# Revit family: P350181-031
name_source: partatom
category: Lighting Fixtures
units: mm (PartAtom-declared; Revit-internal decimal feet)

## family parameters
Cut with Voids When Loaded = No
Host = Face
Light Source = No
OmniClass Number = 23.80.70.11.14.11
OmniClass Title = Downlights
Part Type = Normal
Room Calculation Point = No
Round Connector Dimension = Use Diameter
Shared = No

## types (1)
- P350181-031
    Apparent Load = 60 VA
    Ballast = Paint - Hubbell - Carbon Black
    Certifications = • cCSAus certified to UL 1598
• Wall Mount: Suitable for wet locations
• Surface & Pendant Mount: Suitable for wet
locations under covered ceiling
• Cord Mount and all Wall Wash: Suitable for
damp locations
    Default Elevation = 48 "
    Description = Stockbrace Collection Three-Light Matte Black and Clear Glass Farmhouse Style Flush Mount Ceiling Light
    Features = Application: Inspired by traditional post-and-beam construction, the Stockbrace Collection 3-Light Matte Black Clear Glass Farmhouse Flush Mount Ceiling Light is ideal for any hallway, stairwell, entryway, kitchen, or sitting room.
Styles: Perfect for modern farmhouse style settings.
Finish: The round ceiling plate and stately light bases are coated in a classic matte black finish.
Materials: Constructed from steel to ensure a long product lifespan.
Glass/Shade: Light sources illuminate clear glass shades to complete the clean design.
Bulbs: For ideal illumination, use 3 medium base bulbs that are sold separately (60w max - LED/CFL/incandescent). Compatible with dimmable bulbs.
Dimensions: Measures 12-1/2-inch diameter by 10-inch height.
Certifications: cCSAus damp location listed.
Pairs With: Pairs with the Briarwood, Lockhart, and Clarion collections from Progress Lighting.
Warranty: Our 1-Year Limited Warranty guarantees your complete satisfaction with your purchase and includes professional after-sales customer service support.
    Glass = Paint - Hubbell - White Texture
    Gold = Hubbell - Gold
    Housing Material = Paint - Hubbell - Textured Camera Black
    Lamp = LED/CFL/incandescent
    Manufacturer = Progress Lighting
    Model = P350181-031
    Product Documentation Link = https://hubbellcdn.com
    Product Page URL = https://www.hubbell.com
    Reflector = Glass - Hubbell - Glass
    URL = https://www.hubbell.com
    Voltage = 120 V
    Warranty = 1 year warranty
    Wattage Comments = 60W

## geometry (parser evidence)
native form markers: Blend x3, Sweep x5
no freeform markers — native parametric forms only
